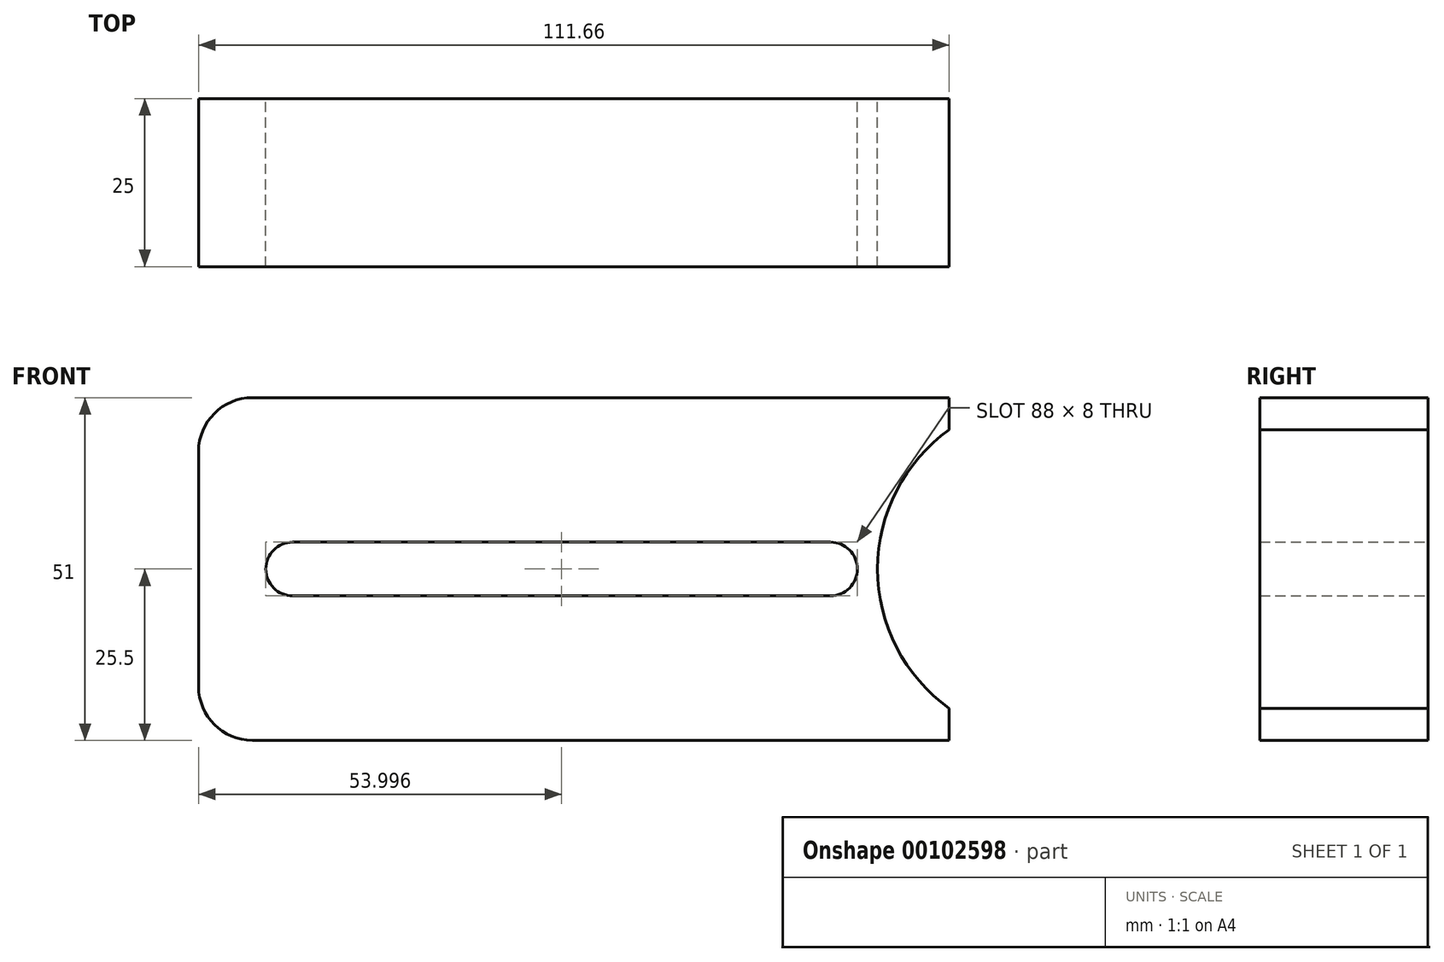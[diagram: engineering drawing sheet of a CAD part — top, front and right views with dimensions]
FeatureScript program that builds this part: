
annotation { "Feature Type Name" : "Feature", "Feature Type Description" : "" }
export const myFeature = defineFeature(function(context is Context, id is Id, definition is map)
    precondition{}
    {
        {
            var Q0;
            Q0=qCreatedBy(makeId("Front.planeOp"),FACE);
            var sketch = newSketch(context, id + "F0", { "sketchPlane" : qUnion([Q0])});
            skLineSegment(sketch, "E0.bottom", {"start": v(-47.83, 25.5) * mm, "end": v(55.83, 25.5) * mm});
            skLineSegment(sketch, "E0.top", {"start": v(-47.83, -25.5) * mm, "end": v(55.83, -25.5) * mm});
            skLineSegment(sketch, "E0.left", {"start": v(-55.83, 17.5) * mm, "end": v(-55.83, -17.5) * mm});
            skLineSegment(sketch, "E0.right", {"start": v(55.83, 25.5) * mm, "end": v(55.83, -25.5) * mm});
            skPoint(sketch, "E0.middle", {"position": v(0, 0) * mm});
            skCircle(sketch, "E1", {"center": v(70.67, 0) * mm, "radius": 25.5 * mm});
            skLineSegment(sketch, "E2", {"start": v(-41.83, 0) * mm, "end": v(38.17, 0) * mm, "construction": true});
            skArc(sketch, "E3.0.startCap", {"start": v(-41.83, -4) * mm, "mid": v(-45.83, 0) * mm, "end": v(-41.83, 4) * mm});
            skArc(sketch, "E3.0.endCap", {"start": v(38.17, 4) * mm, "mid": v(42.17, 0) * mm, "end": v(38.17, -4) * mm});
            skLineSegment(sketch, "E3.0.left", {"start": v(-41.83, 4) * mm, "end": v(38.17, 4) * mm});
            skLineSegment(sketch, "E3.0.right", {"start": v(-41.83, -4) * mm, "end": v(38.17, -4) * mm});
            skPoint(sketch, "E4.visualSharp", {"position": v(-55.83, 25.5) * mm});
            skArc(sketch, "E4.filletArc", {"start": v(-47.83, 25.5) * mm, "mid": v(-53.5, 23.16) * mm, "end": v(-55.83, 17.5) * mm});
            skPoint(sketch, "E5.visualSharp", {"position": v(-55.83, -25.5) * mm});
            skArc(sketch, "E5.filletArc", {"start": v(-55.83, -17.5) * mm, "mid": v(-53.5, -23.16) * mm, "end": v(-47.83, -25.5) * mm});
            skSolve(sketch);
        }
        {
            var Q0;
            {var subQ5=sQuery(id+"F0.wireOp",EDGE,"E0.bottom");Q0=makeQuery(id+"F0.imprint","IMPRINT",FACE,{"disambiguationData":[TD([[makeQuery(id+"F0.imprint","IMPRINT",EDGE,{"derivedFrom":subQ5}),-1.0]])]});}
            extrude(context, id + "F1", {"entities" : qUnion([Q0]), "depth" : 25 * mm});
        }
    });
